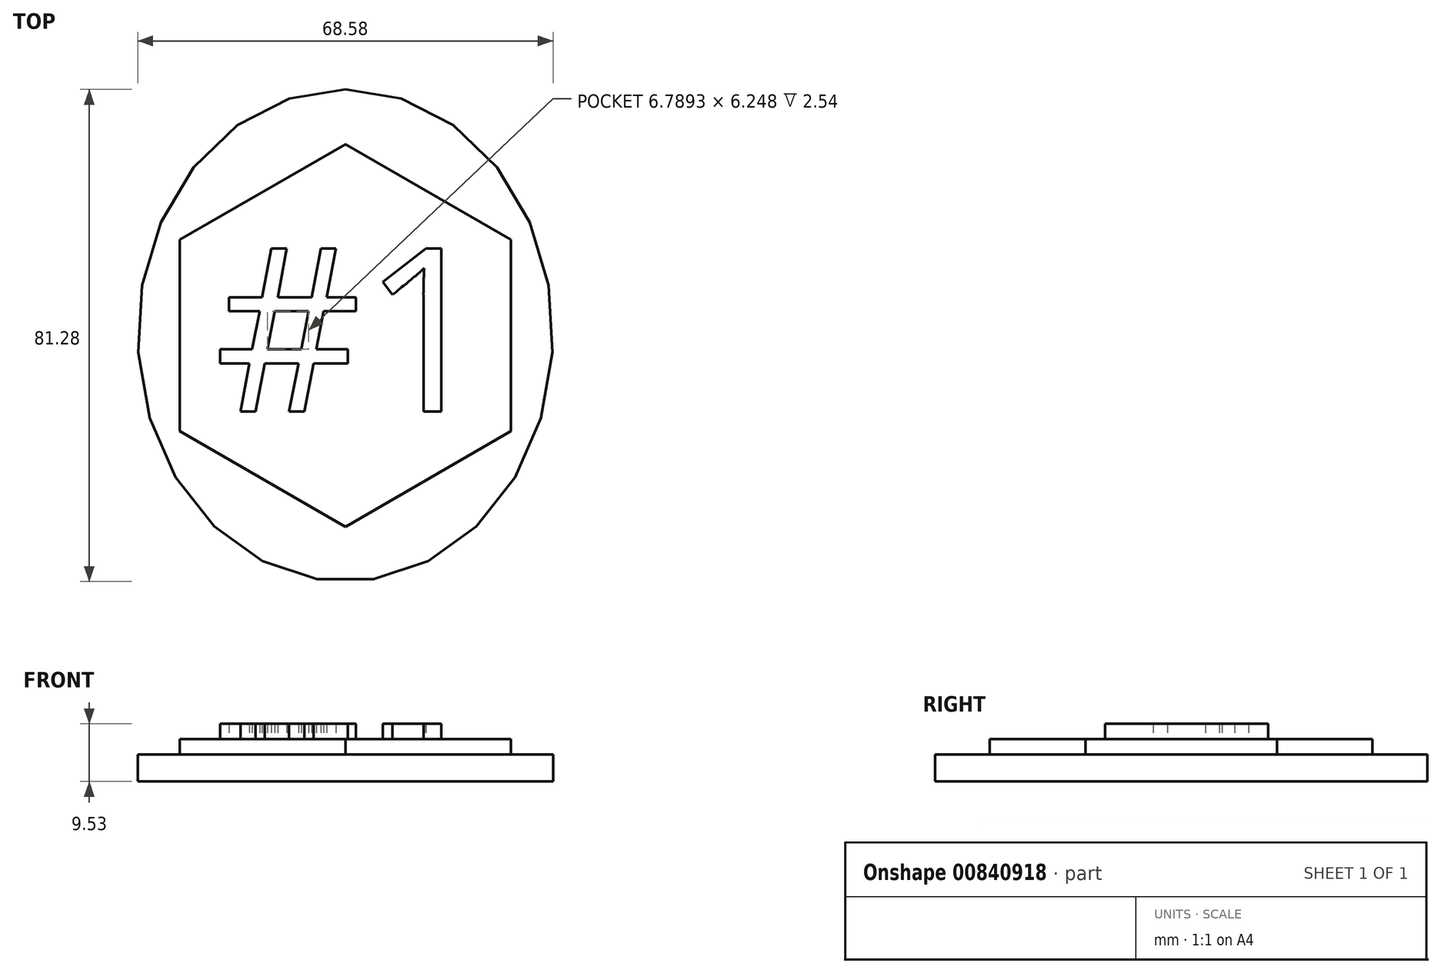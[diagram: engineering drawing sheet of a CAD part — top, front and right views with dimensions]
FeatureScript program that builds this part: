
annotation { "Feature Type Name" : "Feature", "Feature Type Description" : "" }
export const myFeature = defineFeature(function(context is Context, id is Id, definition is map)
    precondition{}
    {
        {
            var Q0;
            Q0=qCreatedBy(makeId("Top.planeOp"),FACE);
            var sketch = newSketch(context, id + "F0", { "sketchPlane" : qUnion([Q0])});
            skEllipse(sketch, "E0", {"center": v(0, 0) * mm, "majorRadius": 40.64 * mm, "minorRadius": 34.3 * mm, "majorAxis": v(0, 1)});
            skSolve(sketch);
        }
        {
            var Q0;
            Q0 = qSketchRegion(id + "F0", true);
            extrude(context, id + "F1", {"entities" : qUnion([Q0]), "depth" : 4.44 * mm, "offsetDistance" : 25.4 * mm});
        }
        {
            var Q0;
            Q0=makeQuery(id+"F1.opExtrude","CAP_FACE",FACE,{"disambiguationData":[OSD([sQuery(id+"F0.wireOp",EDGE,"E0")])],"isStart":false});
            var sketch = newSketch(context, id + "F2", { "sketchPlane" : qUnion([Q0])});
            skCircle(sketch, "E1.cCircle", {"center": v(0, 0) * mm, "radius": 31.6 * mm, "construction": true});
            skLineSegment(sketch, "E1.0", {"start": v(0, 31.6) * mm, "end": v(27.36, 15.8) * mm});
            skLineSegment(sketch, "E1.1", {"start": v(27.36, 15.8) * mm, "end": v(27.36, -15.8) * mm});
            skLineSegment(sketch, "E1.2", {"start": v(27.36, -15.8) * mm, "end": v(0, -31.6) * mm});
            skLineSegment(sketch, "E1.3", {"start": v(0, -31.6) * mm, "end": v(-27.36, -15.8) * mm});
            skLineSegment(sketch, "E1.4", {"start": v(-27.36, -15.8) * mm, "end": v(-27.36, 15.8) * mm});
            skLineSegment(sketch, "E1.5", {"start": v(-27.36, 15.8) * mm, "end": v(0, 31.6) * mm});
            skSolve(sketch);
        }
        {
            var Q0;
            Q0 = qSketchRegion(id + "F2", true);
            extrude(context, id + "F3", {"entities" : qUnion([Q0]), "operationType" : NewBodyOperationType.ADD, "depth" : 2.54 * mm, "offsetDistance" : 25.4 * mm});
        }
        {
            var Q0;
            Q0=makeQuery(id+"F3.opExtrude","CAP_FACE",FACE,{"disambiguationData":[OSD([sQuery(id+"F2.wireOp",EDGE,"E1.0"),sQuery(id+"F2.wireOp",EDGE,"E1.1"),sQuery(id+"F2.wireOp",EDGE,"E1.2"),sQuery(id+"F2.wireOp",EDGE,"E1.3"),sQuery(id+"F2.wireOp",EDGE,"E1.4"),sQuery(id+"F2.wireOp",EDGE,"E1.5")])],"isStart":false});
            var sketch = newSketch(context, id + "F4", { "sketchPlane" : qUnion([Q0])});
            skText(sketch, "E2", { "text": "#1", "fontName": "OpenSans-Regular.ttf"});
            const initialGuessF4  = {"E2": [-0.0216, -0.01254, 1, 0, 0.02711]};
            skSetInitialGuess(sketch, initialGuessF4);
            skSolve(sketch);
        }
        {
            var Q0;
            Q0 = qSketchRegion(id + "F4", true);
            extrude(context, id + "F5", {"entities" : qUnion([Q0]), "operationType" : NewBodyOperationType.ADD, "depth" : 2.54 * mm, "offsetDistance" : 25.4 * mm});
        }
    });
